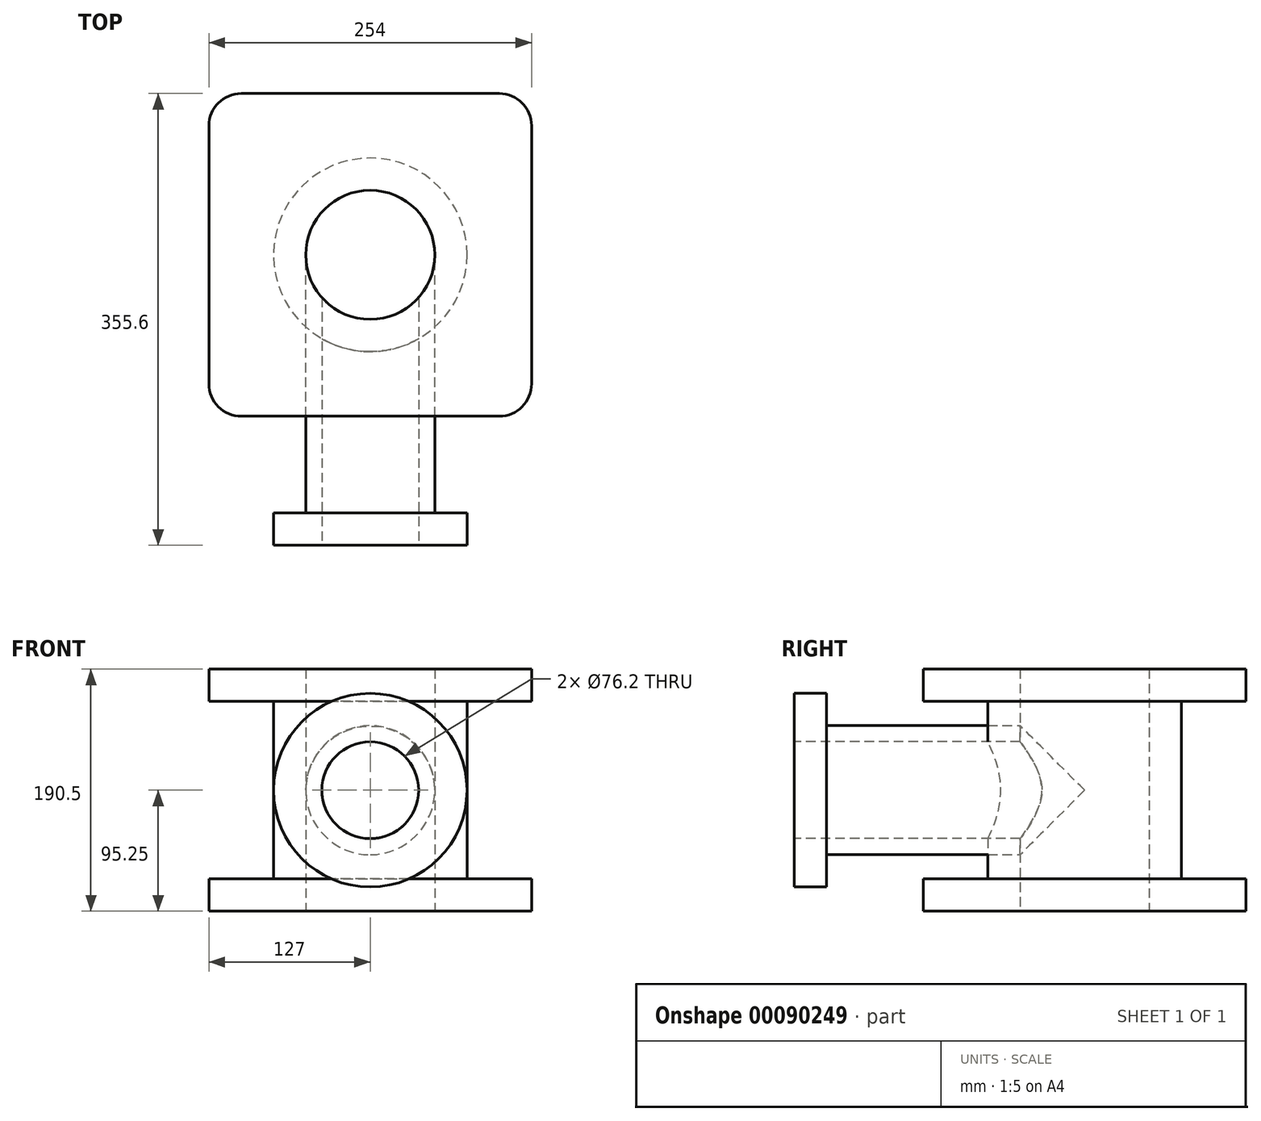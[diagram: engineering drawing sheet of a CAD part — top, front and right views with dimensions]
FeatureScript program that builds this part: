
annotation { "Feature Type Name" : "Feature", "Feature Type Description" : "" }
export const myFeature = defineFeature(function(context is Context, id is Id, definition is map)
    precondition{}
    {
        {
            var Q0;
            Q0=qCreatedBy(makeId("Top.planeOp"),FACE);
            var sketch = newSketch(context, id + "F0", { "sketchPlane" : qUnion([Q0])});
            skCircle(sketch, "E0", {"center": v(0, 0) * mm, "radius": 76.2 * mm});
            skCircle(sketch, "E1", {"center": v(0, 0) * mm, "radius": 50.8 * mm});
            skSolve(sketch);
        }
        {
            var Q0;
            Q0=makeQuery(id+"F0.imprint","IMPRINT",FACE,{"disambiguationData":[TD([[makeQuery(id+"F0.imprint","IMPRINT",EDGE,{"derivedFrom":sQuery(id+"F0.wireOp",EDGE,"E0")}),1.0]])]});
            extrude(context, id + "F1", {"entities" : qUnion([Q0]), "endBound" : BoundingType.SYMMETRIC, "depth" : 139.7 * mm});
        }
        {
            var Q0;
            Q0=makeQuery(id+"F1.opExtrude","CAP_FACE",FACE,{"disambiguationData":[OSD([sQuery(id+"F0.wireOp",EDGE,"E0")])],"isStart":false});
            var sketch = newSketch(context, id + "F2", { "sketchPlane" : qUnion([Q0])});
            skLineSegment(sketch, "E2", {"start": v(0, 127) * mm, "end": v(101.6, 127) * mm});
            skLineSegment(sketch, "E3", {"start": v(127, 101.6) * mm, "end": v(127, 0) * mm});
            skLineSegment(sketch, "E4.MirrorCS", {"start": v(0, 127) * mm, "end": v(-101.6, 127) * mm});
            skLineSegment(sketch, "E5.MirrorCS", {"start": v(-127, 101.6) * mm, "end": v(-127, 0) * mm});
            skLineSegment(sketch, "E6.MirrorCS", {"start": v(-127, -101.6) * mm, "end": v(-127, 0) * mm});
            skLineSegment(sketch, "E7.MirrorCS", {"start": v(0, -127) * mm, "end": v(-101.6, -127) * mm});
            skLineSegment(sketch, "E8.MirrorCS", {"start": v(0, -127) * mm, "end": v(101.6, -127) * mm});
            skLineSegment(sketch, "E9.MirrorCS", {"start": v(127, -101.6) * mm, "end": v(127, 0) * mm});
            skPoint(sketch, "E10.visualSharp", {"position": v(127, 127) * mm});
            skArc(sketch, "E10.filletArc", {"start": v(127, 101.6) * mm, "mid": v(119.56, 119.56) * mm, "end": v(101.6, 127) * mm});
            skPoint(sketch, "E11.visualSharp", {"position": v(-127, 127) * mm});
            skArc(sketch, "E11.filletArc", {"start": v(-101.6, 127) * mm, "mid": v(-119.56, 119.56) * mm, "end": v(-127, 101.6) * mm});
            skPoint(sketch, "E12.visualSharp", {"position": v(-127, -127) * mm});
            skArc(sketch, "E12.filletArc", {"start": v(-127, -101.6) * mm, "mid": v(-119.56, -119.56) * mm, "end": v(-101.6, -127) * mm});
            skPoint(sketch, "E13.visualSharp", {"position": v(127, -127) * mm});
            skArc(sketch, "E13.filletArc", {"start": v(101.6, -127) * mm, "mid": v(119.56, -119.56) * mm, "end": v(127, -101.6) * mm});
            skCircle(sketch, "E14", {"center": v(0, 0) * mm, "radius": 50.8 * mm});
            skSolve(sketch);
        }
        {
            var Q0;
            Q0 = qSketchRegion(id + "F2", true);
            extrude(context, id + "F3", {"entities" : qUnion([Q0]), "operationType" : NewBodyOperationType.ADD, "depth" : 25.4 * mm});
        }
        {
            var Q0;
            Q0=makeQuery(id+"F1.opExtrude","SWEPT_BODY",BODY,{"disambiguationData":[OSD([sQuery(id+"F0.wireOp",EDGE,"E0")])]});
            var Q1;
            Q1=qCreatedBy(makeId("Top.planeOp"),FACE);
            mirror(context, id + "F4", {"operationType" : NewBodyOperationType.ADD, "entities" : qUnion([Q0]), "mirrorPlane" : qUnion([Q1])});
        }
        {
            var Q0;
            Q0=qCreatedBy(makeId("Front.planeOp"),FACE);
            var sketch = newSketch(context, id + "F5", { "sketchPlane" : qUnion([Q0])});
            skCircle(sketch, "E15", {"center": v(0, 0) * mm, "radius": 50.8 * mm});
            skSolve(sketch);
        }
        {
            var Q0;
            Q0 = qSketchRegion(id + "F5", true);
            extrude(context, id + "F6", {"entities" : qUnion([Q0]), "depth" : 203.2 * mm});
        }
        {
            var Q0;
            Q0=makeQuery(id+"F6.opExtrude","CAP_FACE",FACE,{"disambiguationData":[OSD([sQuery(id+"F5.wireOp",EDGE,"E15")])],"isStart":false});
            var sketch = newSketch(context, id + "F7", { "sketchPlane" : qUnion([Q0])});
            skCircle(sketch, "E16", {"center": v(0, 0) * mm, "radius": 76.2 * mm});
            skSolve(sketch);
        }
        {
            var Q0;
            Q0 = qSketchRegion(id + "F7", true);
            extrude(context, id + "F8", {"entities" : qUnion([Q0]), "operationType" : NewBodyOperationType.ADD, "depth" : 25.4 * mm});
        }
        {
            var Q0;
            Q0=makeQuery(id+"F8.opExtrude","CAP_FACE",FACE,{"disambiguationData":[OSD([sQuery(id+"F7.wireOp",EDGE,"E16")])],"isStart":false});
            var sketch = newSketch(context, id + "F9", { "sketchPlane" : qUnion([Q0])});
            skPoint(sketch, "E17", {"position": v(0, 0) * mm});
            skCircle(sketch, "E18", {"center": v(0, 0) * mm, "radius": 38.1 * mm});
            skSolve(sketch);
        }
        {
            var Q0;
            Q0=makeQuery(id+"F0.imprint","IMPRINT",FACE,{"disambiguationData":[TD([[makeQuery(id+"F0.imprint","IMPRINT",EDGE,{"derivedFrom":sQuery(id+"F0.wireOp",EDGE,"E1")}),1.0]])]});
            extrude(context, id + "F10", {"entities" : qUnion([Q0]), "operationType" : NewBodyOperationType.REMOVE, "endBound" : BoundingType.SYMMETRIC, "oppositeDirection" : true, "depth" : 139.7 * mm});
        }
        {
            var Q0;
            Q0 = qSketchRegion(id + "F9", true);
            extrude(context, id + "F11", {"entities" : qUnion([Q0]), "operationType" : NewBodyOperationType.REMOVE, "oppositeDirection" : true, "depth" : 203.2 * mm});
        }
    });
